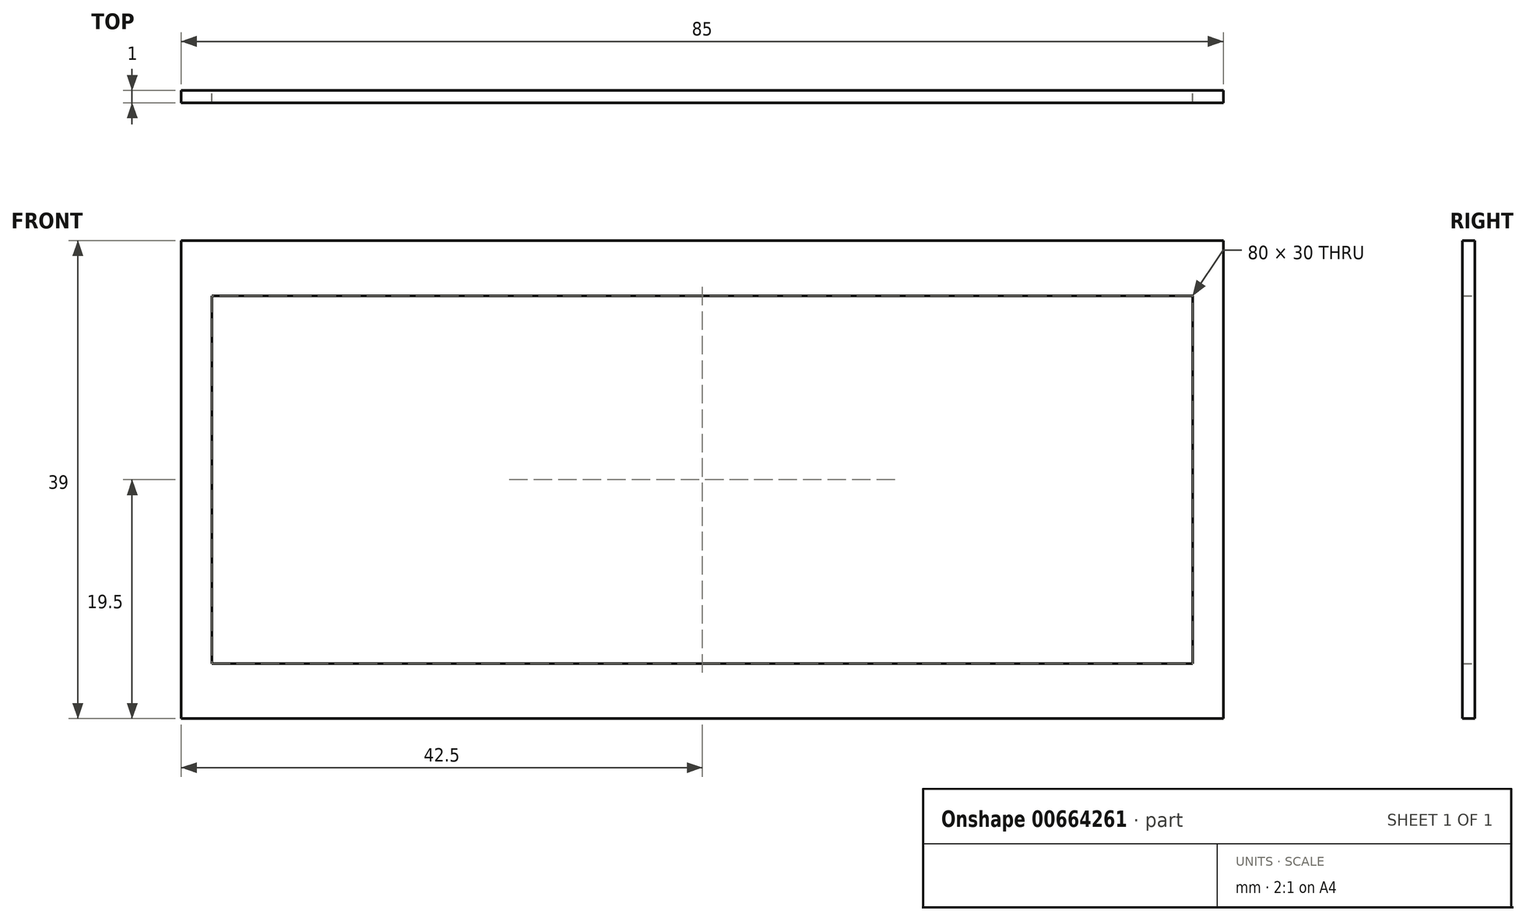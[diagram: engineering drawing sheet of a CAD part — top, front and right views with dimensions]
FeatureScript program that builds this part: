
annotation { "Feature Type Name" : "Feature", "Feature Type Description" : "" }
export const myFeature = defineFeature(function(context is Context, id is Id, definition is map)
    precondition{}
    {
        {
            var Q0;
            Q0=qCreatedBy(makeId("Front.planeOp"),FACE);
            var sketch = newSketch(context, id + "F0", { "sketchPlane" : qUnion([Q0])});
            skLineSegment(sketch, "E0.bottom", {"start": v(40, 15) * mm, "end": v(-40, 15) * mm});
            skLineSegment(sketch, "E0.top", {"start": v(40, -15) * mm, "end": v(-40, -15) * mm});
            skLineSegment(sketch, "E0.left", {"start": v(40, 15) * mm, "end": v(40, -15) * mm});
            skLineSegment(sketch, "E0.right", {"start": v(-40, 15) * mm, "end": v(-40, -15) * mm});
            skPoint(sketch, "E0.middle", {"position": v(0, 0) * mm});
            skLineSegment(sketch, "E1.bottom", {"start": v(42.5, 19.5) * mm, "end": v(-42.5, 19.5) * mm});
            skLineSegment(sketch, "E1.top", {"start": v(42.5, -19.5) * mm, "end": v(-42.5, -19.5) * mm});
            skLineSegment(sketch, "E1.left", {"start": v(42.5, 19.5) * mm, "end": v(42.5, -19.5) * mm});
            skLineSegment(sketch, "E1.right", {"start": v(-42.5, 19.5) * mm, "end": v(-42.5, -19.5) * mm});
            skSolve(sketch);
        }
        {
            var Q0;
            Q0=makeQuery(id+"F0.imprint","IMPRINT",FACE,{"disambiguationData":[TD([[makeQuery(id+"F0.imprint","IMPRINT",EDGE,{"derivedFrom":sQuery(id+"F0.wireOp",EDGE,"E0.bottom")}),-1.0]])]});
            extrude(context, id + "F1", {"entities" : qUnion([Q0]), "depth" : 1 * mm, "offsetDistance" : 25 * mm});
        }
    });
